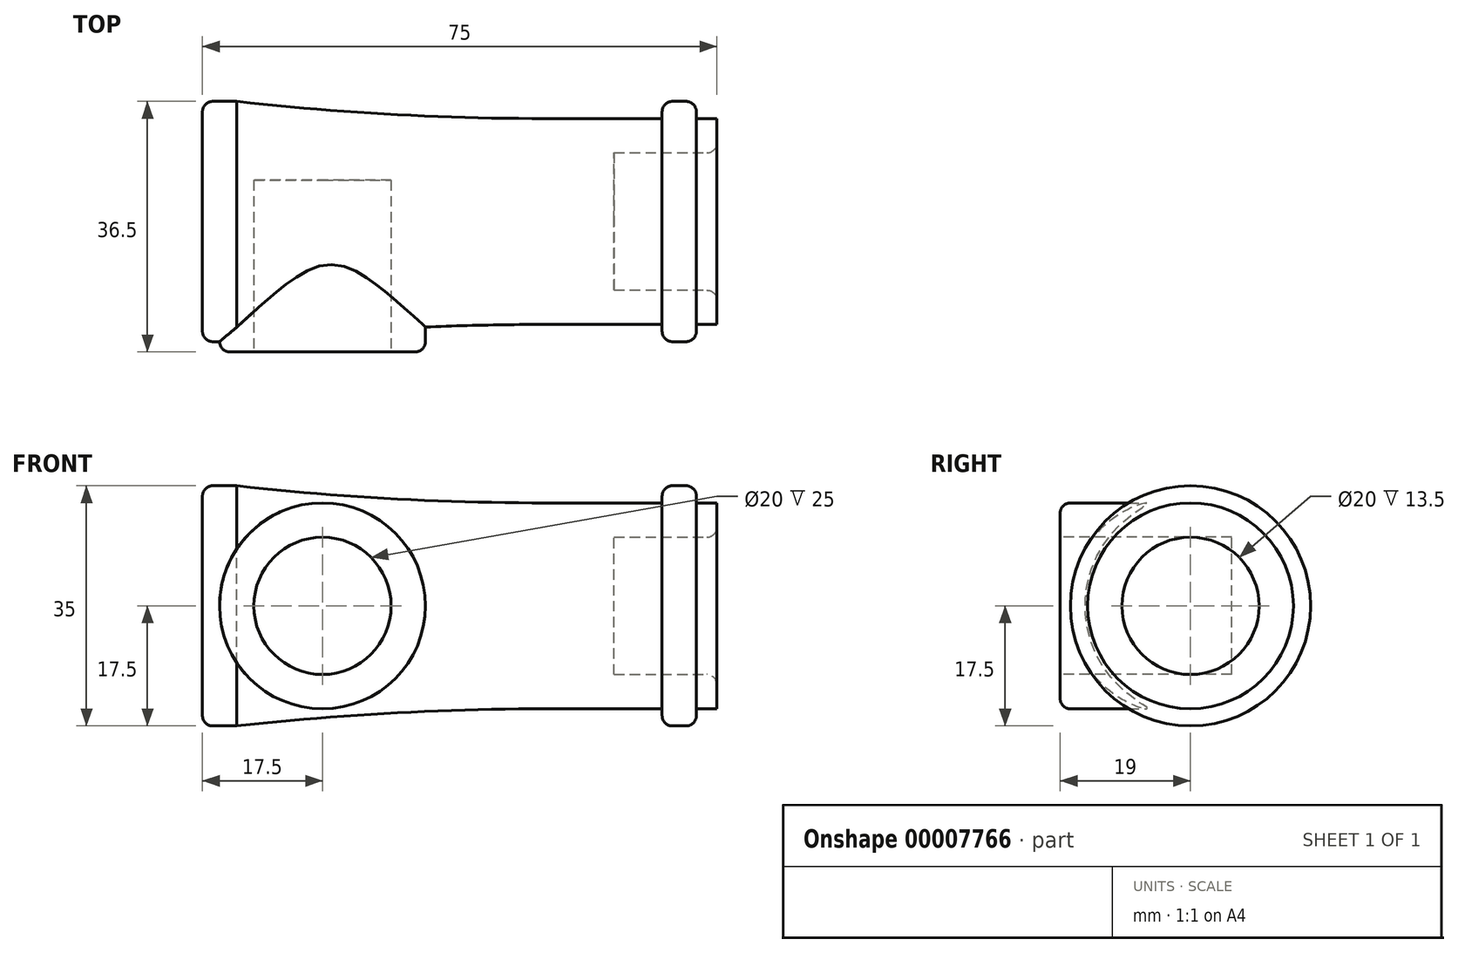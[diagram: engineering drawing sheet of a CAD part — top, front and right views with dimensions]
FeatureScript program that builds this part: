
annotation { "Feature Type Name" : "Feature", "Feature Type Description" : "" }
export const myFeature = defineFeature(function(context is Context, id is Id, definition is map)
    precondition{}
    {
        {
            var Q0;
            Q0=qCreatedBy(makeId("Front.planeOp"),FACE);
            var sketch = newSketch(context, id + "F0", { "sketchPlane" : qUnion([Q0])});
            skLineSegment(sketch, "E0.top", {"start": v(50, 15) * mm, "end": v(67, 15) * mm});
            skLineSegment(sketch, "E0.right", {"start": v(75, 10) * mm, "end": v(75, 15) * mm});
            skLineSegment(sketch, "E1", {"start": v(5, 17.5) * mm, "end": v(0, 17.5) * mm});
            skLineSegment(sketch, "E2", {"start": v(0, 17.5) * mm, "end": v(0, 0) * mm});
            skLineSegment(sketch, "E3", {"start": v(60, 0) * mm, "end": v(0, 0) * mm});
            skArc(sketch, "E4", {"start": v(5, 17.5) * mm, "mid": v(27.47, 15.63) * mm, "end": v(50, 15) * mm});
            skLineSegment(sketch, "E5", {"start": v(67, 15) * mm, "end": v(67, 17.5) * mm});
            skLineSegment(sketch, "E6", {"start": v(67, 17.5) * mm, "end": v(72, 17.5) * mm});
            skLineSegment(sketch, "E7", {"start": v(72, 17.5) * mm, "end": v(72, 15) * mm});
            skLineSegment(sketch, "E8.trimOffspring", {"start": v(72, 15) * mm, "end": v(75, 15) * mm});
            skLineSegment(sketch, "E9.top", {"start": v(75, 10) * mm, "end": v(60, 10) * mm});
            skLineSegment(sketch, "E9.right", {"start": v(60, 0) * mm, "end": v(60, 10) * mm});
            skSolve(sketch);
        }
        {
            var Q0;
            Q0 = qSketchRegion(id + "F0", true);
            var Q1;
            Q1=sQuery(id+"F0.wireOp",EDGE,"E3");
            revolve(context, id + "F1", {"entities" : qUnion([Q0]), "axis" : qUnion([Q1]), "revolveType" : RevolveType.FULL});
        }
        {
            var Q0;
            Q0=qCreatedBy(makeId("Front.planeOp"),FACE);
            var sketch = newSketch(context, id + "F2", { "sketchPlane" : qUnion([Q0])});
            skCircle(sketch, "E10", {"center": v(17.5, 0) * mm, "radius": 15 * mm});
            skSolve(sketch);
        }
        {
            var Q0;
            Q0 = qSketchRegion(id + "F2", true);
            extrude(context, id + "F3", {"entities" : qUnion([Q0]), "operationType" : NewBodyOperationType.ADD, "depth" : 19 * mm});
        }
        {
            var Q0;
            Q0=makeQuery(id+"F3.opExtrude","CAP_FACE",FACE,{"disambiguationData":[OSD([sQuery(id+"F2.wireOp",EDGE,"E10")])],"isStart":false});
            var sketch = newSketch(context, id + "F4", { "sketchPlane" : qUnion([Q0])});
            skCircle(sketch, "E11", {"center": v(17.5, 0) * mm, "radius": 10 * mm});
            skSolve(sketch);
        }
        {
            var Q0;
            Q0 = qSketchRegion(id + "F4", true);
            extrude(context, id + "F5", {"entities" : qUnion([Q0]), "operationType" : NewBodyOperationType.REMOVE, "oppositeDirection" : true, "depth" : 25 * mm});
        }
        {
            var Q0;
            Q0=makeQuery(id+"F3.opExtrude","CAP_EDGE",EDGE,{"disambiguationData":[OSD([sQuery(id+"F2.wireOp",EDGE,"E10")])],"isStart":false});
            var Q1;
            Q1=makeQuery(id+"F1.opRevolve","SWEPT_EDGE",EDGE,{"disambiguationData":[OSD([sQuery(id+"F0.wireOp",EDGE,"E1"),sQuery(id+"F0.wireOp",EDGE,"E2")])]});
            var Q2;
            Q2=makeQuery(id+"F1.opRevolve","SWEPT_EDGE",EDGE,{"disambiguationData":[OSD([sQuery(id+"F0.wireOp",EDGE,"E5"),sQuery(id+"F0.wireOp",EDGE,"E6")])]});
            var Q3;
            Q3=makeQuery(id+"F1.opRevolve","SWEPT_EDGE",EDGE,{"disambiguationData":[OSD([sQuery(id+"F0.wireOp",EDGE,"E6"),sQuery(id+"F0.wireOp",EDGE,"E7")])]});
            var Q4;
            Q4=makeQuery(id+"F1.opRevolve","SWEPT_EDGE",EDGE,{"disambiguationData":[OSD([sQuery(id+"F0.wireOp",EDGE,"E0.right"),sQuery(id+"F0.wireOp",EDGE,"E9.top")])]});
            fillet(context, id + "F6", {"entities" : qUnion([Q0, Q1, Q2, Q3, Q4]), "radius" : 1.5 * mm, "tangentPropagation" : true, "allowEdgeOverflow" : false});
        }
    });
